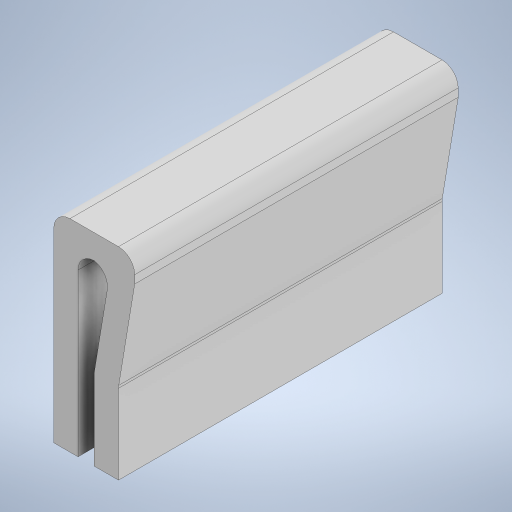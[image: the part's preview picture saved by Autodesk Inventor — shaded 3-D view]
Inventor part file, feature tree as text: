
AUTODESK INVENTOR PART (.ipt)
format: ipt  version: 2024 (Build 280153000, 153)  size: 222,208 bytes
history: native  units: mm
features: other x1, extrude x1, fillet x1, sketch x1
ambient origin geometry x8: Origin, YZ Plane, XZ Plane, XY Plane, X Axis, Y Axis, Z Axis, Center Point
bodies: Body1 (feature_tree)
feature tree (4):
  other  "ソリッド1"
  extrude  "押し出し1"  Depth=10.0mm
  fillet  "フィレット1"  [1 undecoded]
  sketch  "スケッチ1"
note: 1 required parameter value undecoded (feature->parameter linkage not recoverable at this tier; creation-order binding heuristic only, values carry confidence <= 0.55)
